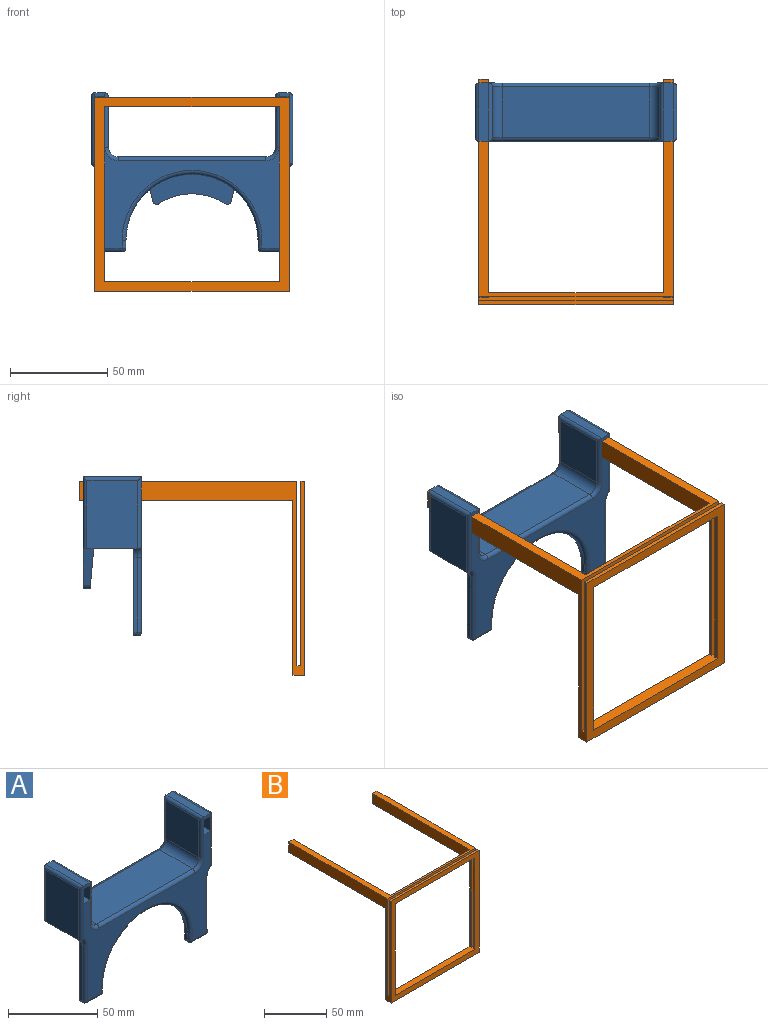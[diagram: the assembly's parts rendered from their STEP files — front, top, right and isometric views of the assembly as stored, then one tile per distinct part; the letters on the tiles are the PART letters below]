
ASSEMBLY  parts=2 mates=1
PART A: 76 faces, bbox 104x30x82 mm
  f0: plane 5x2mm, normal (0,-1,0), area 10mm2, adj f16,f23,f46,f53
  f1: plane 5x2mm, normal (0,-1,0), area 10mm2, adj f18,f21,f39,f58
  f2: plane 5x2mm, normal (0,1,0), area 10mm2, adj f16,f23,f50,f51
  f3: plane 5x2mm, normal (0,1,0), area 10mm2, adj f18,f21,f43,f54
  f4: plane 11x2mm, normal (0,0,-1), area 22mm2, adj f29,f59,f66,f70
  f5: plane 49x0.19mm, normal (0,-1,0), area 9.1mm2, adj f6,f7,f14,f27
  f6: plane 18.94x5.5mm, normal (0.97,0,-0.22), area 90mm2, adj f5,f9,f14,f27,f75
  f7: plane 18.94x5.5mm, normal (-0.97,0,-0.22), area 90mm2, adj f5,f9,f14,f27,f74
  f8: cylinder r=31mm len=34.25mm, axis (0,1,0), area 143.6mm2, adj f9,f27,f74,f75
  f9: plane 100x45.29mm, normal (0,1,0), area 1224.7mm2, adj f6,f7,f8,f14,f19,f25,f43,f45
  f10: plane 100x67.8mm, normal (0,-1,0), area 2170.6mm2, adj f19,f25,f39,f40,f42,f44,f46,f53
  f11: plane 76x26mm, normal (0,0,1), area 1976mm2, adj f37,f38,f42,f47
  f12: plane 35x26mm, normal (-1,0,0), area 910mm2, adj f14,f35,f51,f52,f53
  f13: plane 35x26mm, normal (1,0,0), area 910mm2, adj f14,f36,f54,f56,f58
  f14: plane 104x26mm, normal (0,0,-1), area 2432.8mm2, adj f5,f6,f7,f9,f12,f13,f29,f51
  f15: plane 26x26mm, normal (1,0,0), area 676mm2, adj f38,f46,f48,f50
  f16: plane 30x5mm, normal (0,0,1), area 150mm2, adj f0,f2,f48,f52
  f17: plane 26x26mm, normal (-1,0,0), area 676mm2, adj f37,f39,f41,f43
  f18: plane 30x5mm, normal (0,0,1), area 150mm2, adj f1,f3,f41,f56
  f19: plane 30x5.2mm, normal (0,0,1), area 156mm2, adj f9,f10,f20,f22,f39,f43,f54,f58
  f20: plane 30x10.2mm, normal (-1,0,0), area 305.9mm2, adj f19,f21,f54,f58
  f21: plane 30x5.2mm, normal (0,0,-1), area 156mm2, adj f1,f3,f20,f22,f39,f43,f54,f58
  f22: plane 30x10.2mm, normal (1,0,0), area 305.9mm2, adj f19,f21,f39,f43
  f23: plane 30x5.2mm, normal (0,0,-1), area 156mm2, adj f0,f2,f24,f26,f46,f50,f51,f53
  f24: plane 30x10.2mm, normal (1,0,0), area 305.9mm2, adj f23,f25,f51,f53
  f25: plane 30x5.2mm, normal (0,0,1), area 156mm2, adj f9,f10,f24,f26,f46,f50,f51,f53
  f26: plane 30x10.2mm, normal (-1,0,0), area 305.9mm2, adj f23,f25,f46,f50
  f27: plane 48.92x20.3mm, normal (0,-1,-0.09), area 769.9mm2, adj f5,f6,f7,f8,f74,f75
  f28: plane 38.42x2mm, normal (-1,0,0), area 76.8mm2, adj f29,f35,f57,f66
  f29: plane 104x45mm, normal (0,1,0), area 2190.4mm2, adj f4,f14,f28,f30,f31,f32,f33,f34
  f30: plane 38.42x2mm, normal (1,0,0), area 76.8mm2, adj f29,f36,f62,f68
  f31: plane 11x2mm, normal (0,0,-1), area 22mm2, adj f29,f64,f68,f72
  f32: plane 4x2mm, normal (-1,0,0), area 8mm2, adj f29,f33,f65,f72
  f33: cylinder r=34mm len=68mm, axis (0,-1,0), area 213.6mm2, adj f29,f32,f34,f63
  f34: plane 4x2mm, normal (1,0,0), area 8mm2, adj f29,f33,f61,f70
  f35: cylinder r=5mm len=4.58mm, axis (0,1,0), area 11.6mm2, adj f12,f28,f29,f55
  f36: cylinder r=5mm len=4.58mm, axis (0,1,0), area 11.6mm2, adj f13,f29,f30,f60
  f37: cylinder r=5mm len=26mm, axis (0,-1,0), area 204.2mm2, adj f11,f17,f40,f45
  f38: cylinder r=5mm len=26mm, axis (0,1,0), area 204.2mm2, adj f11,f15,f44,f49
  f39: cylinder r=2mm len=28mm, axis (0,0,1), area 84.7mm2, adj f1,f10,f17,f19,f21,f22,f40,f41
  f40: torus R=7mm, axis (0,1,0), area 28.3mm2, adj f10,f37,f39,f42
  f41: cylinder r=2mm len=30mm, axis (0,1,0), area 89.7mm2, adj f17,f18,f39,f43
  f42: cylinder r=2mm len=76mm, axis (-1,0,0), area 238.8mm2, adj f10,f11,f40,f44
  f43: cylinder r=2mm len=28mm, axis (0,0,-1), area 84.7mm2, adj f3,f9,f17,f19,f21,f22,f41,f45
  f44: torus R=7mm, axis (0,1,0), area 28.3mm2, adj f10,f38,f42,f46
  f45: torus R=7mm, axis (0,1,0), area 28.3mm2, adj f9,f37,f43,f47
  f46: cylinder r=2mm len=28mm, axis (0,0,-1), area 84.7mm2, adj f0,f10,f15,f23,f25,f26,f44,f48
  f47: cylinder r=2mm len=76mm, axis (1,0,0), area 238.8mm2, adj f9,f11,f45,f49
  f48: cylinder r=2mm len=30mm, axis (0,-1,0), area 89.7mm2, adj f15,f16,f46,f50
  f49: torus R=7mm, axis (0,1,0), area 28.3mm2, adj f9,f38,f47,f50
  f50: cylinder r=2mm len=28mm, axis (0,0,1), area 84.7mm2, adj f2,f9,f15,f23,f25,f26,f48,f49
  f51: cylinder r=2mm len=37mm, axis (0,0,1), area 112.9mm2, adj f2,f9,f12,f14,f23,f24,f25,f52
  f52: cylinder r=2mm len=30mm, axis (0,1,0), area 89.7mm2, adj f12,f16,f51,f53
  f53: cylinder r=2mm len=37mm, axis (0,0,-1), area 111.6mm2, adj f0,f10,f12,f23,f24,f25,f52,f55
  f54: cylinder r=2mm len=37mm, axis (0,0,-1), area 112.9mm2, adj f3,f9,f13,f14,f19,f20,f21,f56
  f55: torus R=7mm, axis (0,1,0), area 19.3mm2, adj f10,f35,f53,f57
  f56: cylinder r=2mm len=30mm, axis (0,-1,0), area 89.7mm2, adj f13,f18,f54,f58
  f57: cylinder r=2mm len=38.42mm, axis (0,0,1), area 120.7mm2, adj f10,f28,f55,f67
  f58: cylinder r=2mm len=37mm, axis (0,0,1), area 111.6mm2, adj f1,f10,f13,f19,f20,f21,f56,f60
  f59: cylinder r=2mm len=11mm, axis (-1,0,0), area 34.6mm2, adj f4,f10,f67,f71
  f60: torus R=7mm, axis (0,1,0), area 19.3mm2, adj f10,f36,f58,f62
  f61: cylinder r=2mm len=4mm, axis (0,0,-1), area 12.6mm2, adj f10,f34,f63,f71
  f62: cylinder r=2mm len=38.42mm, axis (0,0,-1), area 120.7mm2, adj f10,f30,f60,f69
  f63: torus R=36mm, axis (0,1,0), area 342.7mm2, adj f10,f33,f61,f65
  f64: cylinder r=2mm len=11mm, axis (-1,0,0), area 34.6mm2, adj f10,f31,f69,f73
  f65: cylinder r=2mm len=4mm, axis (0,0,1), area 12.6mm2, adj f10,f32,f63,f73
  f66: cylinder r=2mm len=2mm, axis (0,-1,0), area 6.3mm2, adj f4,f28,f29,f67
  f67: sphere r=2mm, area 6.3mm2, adj f57,f59,f66
  f68: cylinder r=2mm len=2mm, axis (0,1,0), area 6.3mm2, adj f29,f30,f31,f69
  f69: sphere r=2mm, area 6.3mm2, adj f62,f64,f68
  f70: cylinder r=2mm len=2mm, axis (0,1,0), area 6.3mm2, adj f4,f29,f34,f71
  f71: sphere r=2mm, area 6.3mm2, adj f59,f61,f70
  f72: cylinder r=2mm len=2mm, axis (0,-1,0), area 6.3mm2, adj f29,f31,f32,f73
  f73: sphere r=2mm, area 6.3mm2, adj f64,f65,f72
  f74: cylinder r=2mm len=3.75mm, axis (0,1,0), area 14.1mm2, adj f7,f8,f9,f27
  f75: cylinder r=2mm len=3.75mm, axis (0,1,0), area 14.1mm2, adj f6,f8,f9,f27
PART B: 21 faces, bbox 100x116x100 mm
  f0: plane 90x5mm, normal (0,1,0), area 450mm2, adj f2,f3,f4,f5
  f1: plane 100x90mm, normal (0,1,0), area 1350mm2, adj f3,f5,f6,f10,f11,f12,f17,f19
  f2: plane 112x100mm, normal (0,0,1), area 1300mm2, adj f0,f3,f5,f10,f12,f15,f18,f20
  f3: plane 112x95mm, normal (1,0,0), area 1280mm2, adj f0,f1,f2,f4,f6,f15,f19,f20
  f4: plane 90x2mm, normal (0,0,-1), area 180mm2, adj f0,f3,f5,f15
  f5: plane 112x95mm, normal (-1,0,0), area 1280mm2, adj f0,f1,f2,f4,f6,f15,f17,f18
  f6: plane 100x6mm, normal (0,0,1), area 560mm2, adj f1,f3,f5,f7,f10,f12,f13,f14
  f7: plane 90x2mm, normal (1,0,0), area 180mm2, adj f6,f8,f14,f16
  f8: plane 90x2mm, normal (0,0,-1), area 180mm2, adj f7,f13,f14,f16
  f9: plane 100x2mm, normal (0,0,1), area 200mm2, adj f10,f12,f14,f16
  f10: plane 116x100mm, normal (-1,0,0), area 1510mm2, adj f1,f2,f6,f9,f11,f14,f15,f16
  f11: plane 100x6mm, normal (0,0,-1), area 600mm2, adj f1,f10,f12,f14
  f12: plane 116x100mm, normal (1,0,0), area 1510mm2, adj f1,f2,f6,f9,f11,f14,f15,f16
  f13: plane 90x2mm, normal (-1,0,0), area 180mm2, adj f6,f8,f14,f16
  f14: plane 100x100mm, normal (0,-1,0), area 1900mm2, adj f6,f7,f8,f9,f10,f11,f12,f13
  f15: plane 100x95mm, normal (0,-1,0), area 1400mm2, adj f2,f3,f4,f5,f6,f10,f12
  f16: plane 100x95mm, normal (0,1,0), area 1400mm2, adj f6,f7,f8,f9,f10,f12,f13
  f17: plane 110x5mm, normal (0,0,-1), area 550mm2, adj f1,f5,f12,f18
  f18: plane 10x5mm, normal (0,1,0), area 50mm2, adj f2,f5,f12,f17
  f19: plane 110x5mm, normal (0,0,-1), area 550mm2, adj f1,f3,f10,f20
  f20: plane 10x5mm, normal (0,1,0), area 50mm2, adj f2,f3,f10,f19
PLACE A t=(-7.6,-18.98,-9.31)mm
PLACE B t=(-6.79,-119.1,-73.95)mm
MATE slider B.f18 <-> A.f10  axis (0,1,0) through (39.9,-9.1,15.49)mm
